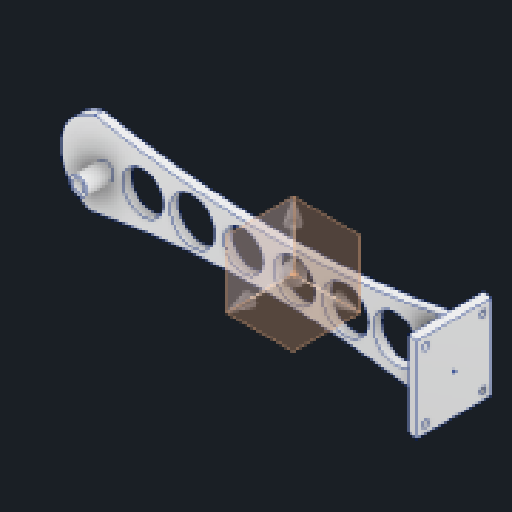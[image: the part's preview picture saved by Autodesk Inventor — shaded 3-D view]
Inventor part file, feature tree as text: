
AUTODESK INVENTOR PART (.ipt)
format: ipt  version: 2023.4 (Build 274418000, 418)  size: 218,624 bytes
history: native  units: mm
features: sketch x14, extrude x8
ambient origin geometry x8: Origin, YZ Plane, XZ Plane, XY Plane, X Axis, Y Axis, Z Axis, Center Point
bodies: Solid1 (feature_tree)
feature tree (22):
  extrude  "Extrusion1"  Depth=40.0mm
  extrude  "Extrusion2"  Depth=400.0mm
  extrude  "Extrusion3"  Depth=4.0mm TaperAngle=0.0deg
  extrude  "Extrusion4"  Depth=11.9mm TaperAngle=0.0deg
  extrude  "Extrusion5"  Depth=5.0mm TaperAngle=0.0deg
  sketch  "Sketch6"  dims[d19=15.0mm d20=0.0mm d21=35.0mm d22=0.0mm]
  sketch  "Sketch7"  dims[d23=19.0mm d24=0.0mm d27=2.95mm]
  sketch  "Sketch8"  dims[d28=2.95mm d29=2.95mm]
  extrude  "Extrusion6"  Depth=15.0mm TaperAngle=0.0deg
  sketch  "Sketch10"  dims[d31=4.0mm]
  sketch  "Sketch11"  dims[d32=4.0mm]
  sketch  "Sketch12"  dims[d33=4.0mm]
  extrude  "Extrusion7"  Depth=19.0mm
  extrude  "Extrusion8"  Depth=2.95mm
  sketch  "Sketch1"  dims[d5=40.0mm d6=40.0mm]
  sketch  "Sketch2"  dims[d7=150.0mm d8=400.0mm]
  sketch  "Sketch3"  dims[d9=400.0mm d10=4.0mm d11=0.0mm]
  sketch  "Sketch4"  dims[d12=8.0mm d13=10.75mm d14=11.9mm d15=0.0mm]
  sketch  "Sketch5"  dims[d16=5.5mm d17=5.0mm d18=0.0mm]
  sketch  "Sketch9"  dims[d30=2.95mm]
  sketch  "Sketch13"  dims[d34=4.0mm]
  sketch  "Sketch14"  dims[d35=4.0mm d36=4.0mm d37=4.0mm d38=4.0mm d39=5.0mm d40=0.0mm d41=10.0mm d42=0.0mm d43=1.0mm d44=1.0mm d45=0.1mm d46=0.0mm]
